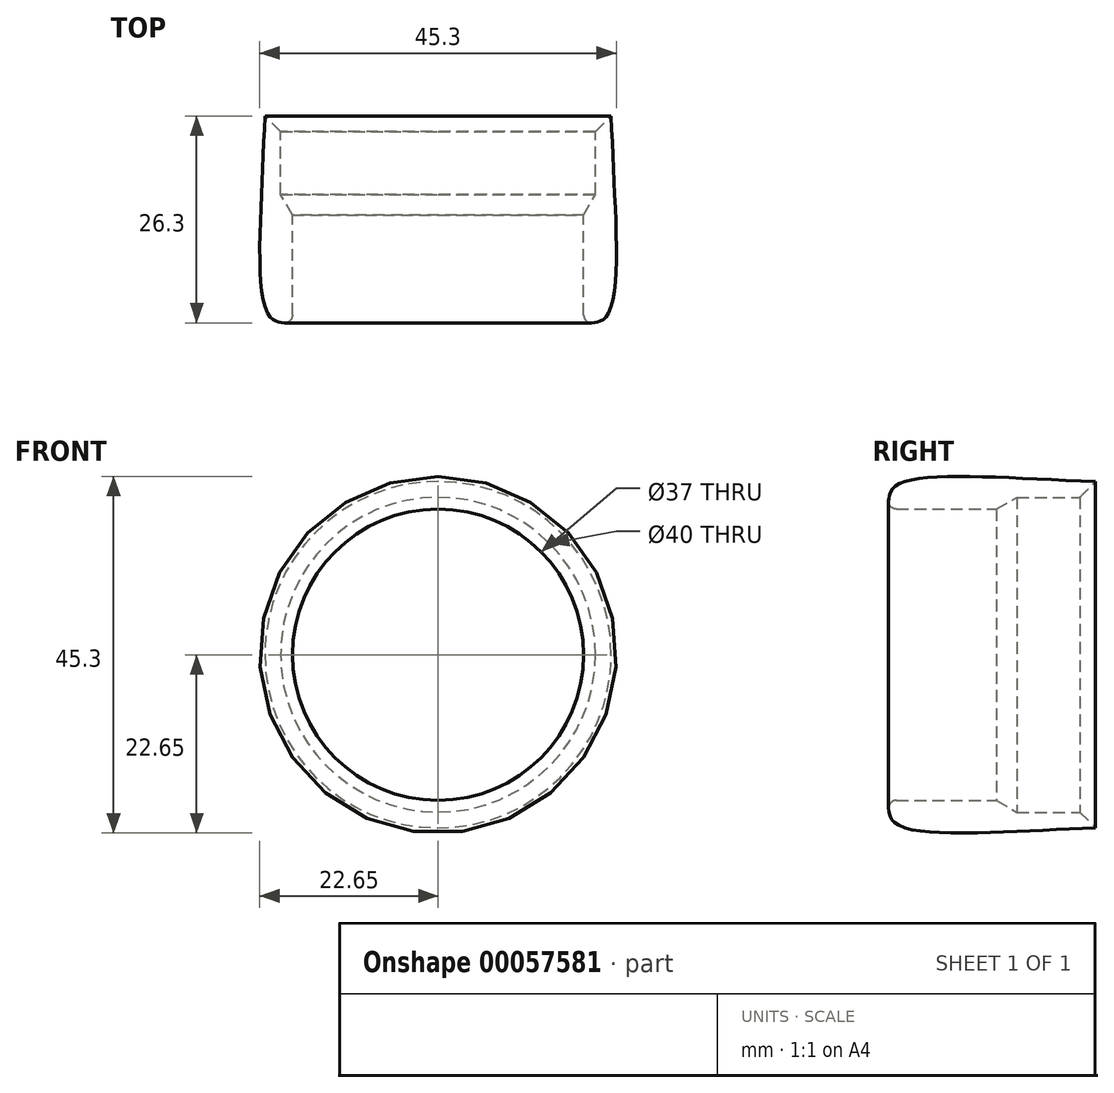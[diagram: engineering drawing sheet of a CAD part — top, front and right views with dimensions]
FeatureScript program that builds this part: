
annotation { "Feature Type Name" : "Feature", "Feature Type Description" : "" }
export const myFeature = defineFeature(function(context is Context, id is Id, definition is map)
    precondition{}
    {
        {
            var Q0;
            Q0=qCreatedBy(makeId("Right.planeOp"),FACE);
            var sketch = newSketch(context, id + "F0", { "sketchPlane" : qUnion([Q0])});
            skLineSegment(sketch, "E0", {"start": v(0, 0) * mm, "end": v(-16.3, 0) * mm});
            skLineSegment(sketch, "E1", {"start": v(-2.6, 18.5) * mm, "end": v(-16.3, 18.5) * mm});
            skLineSegment(sketch, "E2", {"start": v(0, 20) * mm, "end": v(10, 20) * mm});
            skLineSegment(sketch, "E3", {"start": v(10, 20) * mm, "end": v(10, 22) * mm});
            skLineSegment(sketch, "E4", {"start": v(-16.3, 18.5) * mm, "end": v(-16.3, 19.5) * mm});
            skFitSpline(sketch, "E5", {"points": [v(-16.3, 19.5) * mm, v(-15.3, 21.5) * mm, v(10, 22) * mm], "startDerivative": vector(0, 7.35) * mm, "endDerivative": vector(43.53, -1.5) * mm});
            skLineSegment(sketch, "E6", {"start": v(-2.6, 18.5) * mm, "end": v(0, 20) * mm});
            skSolve(sketch);
        }
        {
            var Q0;
            Q0=makeQuery(id+"F0.imprint","IMPRINT",FACE,{"disambiguationData":[TD([[makeQuery(id+"F0.imprint","IMPRINT",EDGE,{"derivedFrom":sQuery(id+"F0.wireOp",EDGE,"E1")}),-1.0]])]});
            var Q1;
            Q1=sQuery(id+"F0.wireOp",EDGE,"E0");
            revolve(context, id + "F1", {"entities" : qUnion([Q0]), "axis" : qUnion([Q1]), "revolveType" : RevolveType.FULL});
        }
        {
            var Q0;
            Q0=makeQuery(id+"F1.opRevolve","SWEPT_EDGE",EDGE,{"disambiguationData":[OSD([sQuery(id+"F0.wireOp",EDGE,"E1"),sQuery(id+"F0.wireOp",EDGE,"E4")])]});
            fillet(context, id + "F2", {"entities" : qUnion([Q0]), "radius" : 1 * mm, "tangentPropagation" : true, "allowEdgeOverflow" : false});
        }
        {
            var Q0;
            Q0=makeQuery(id+"F1.opRevolve","SWEPT_EDGE",EDGE,{"disambiguationData":[OSD([sQuery(id+"F0.wireOp",EDGE,"E2"),sQuery(id+"F0.wireOp",EDGE,"E3")])]});
            chamfer(context, id + "F3", {"entities" : qUnion([Q0]), "width" : 2 * mm, "tangentPropagation" : true});
        }
    });
